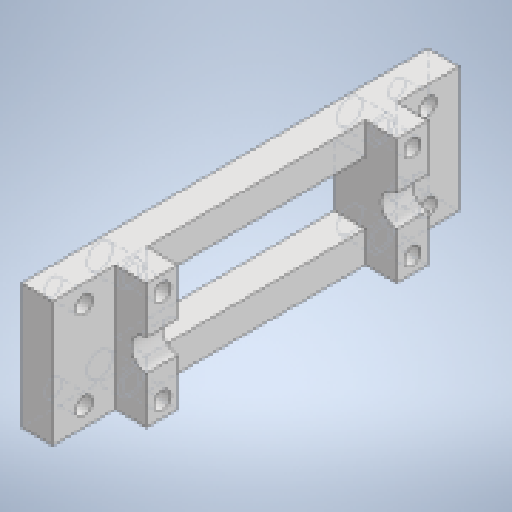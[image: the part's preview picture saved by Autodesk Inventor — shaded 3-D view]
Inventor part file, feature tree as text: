
AUTODESK INVENTOR PART (.ipt)
format: ipt  version: 2023 (Build 270158000, 158)  size: 243,712 bytes
history: native  units: mm
features: extrude x6, sketch x6
ambient origin geometry x8: Origin, YZ Plane, XZ Plane, XY Plane, X Axis, Y Axis, Z Axis, Center Point
bodies: Solid1 (feature_tree)
feature tree (12):
  extrude  "Extrusion1"  Depth=5.0mm
  extrude  "Extrusion2"  Depth=15.0mm
  extrude  "Extrusion3"  Depth=35.0mm
  extrude  "Extrusion4"  Depth=10.0mm
  extrude  "Extrusion5"  Depth=10.0mm
  extrude  "Extrusion6"  Depth=5.0mm TaperAngle=0.0deg
  sketch  "Sketch1"  dims[d0=5.0mm d1=5.0mm]
  sketch  "Sketch2"  dims[d2=5.0mm d3=15.0mm]
  sketch  "Sketch3"  dims[d4=15.0mm d5=35.0mm]
  sketch  "Sketch4"  dims[d6=20.0mm d7=0.0mm d8=10.0mm]
  sketch  "Sketch5"  dims[d9=10.0mm d10=10.0mm]
  sketch  "Sketch6"  dims[d11=5.0mm d12=200.0mm d13=0.0mm d14=5.0mm d15=5.0mm d16=20.0mm d17=0.0mm d18=10.0mm d19=10.0mm d20=3.0mm d21=3.0mm d22=5.0mm d23=5.0mm d24=5.0mm d25=5.0mm d26=3.0mm d27=3.0mm d28=2.75mm d29=2.75mm d30=2.75mm d31=2.75mm d32=5.0mm d33=0.0mm d34=2.5mm d35=2.5mm d36=2.5mm d37=2.5mm d38=2.5mm d39=2.5mm d40=2.5mm d41=2.5mm d42=2.75mm d43=2.75mm d44=2.75mm d45=2.75mm d46=15.0mm d47=0.0mm d48=4.0mm d49=4.0mm d50=4.0mm d51=4.0mm d52=5.0mm d53=0.0mm]
